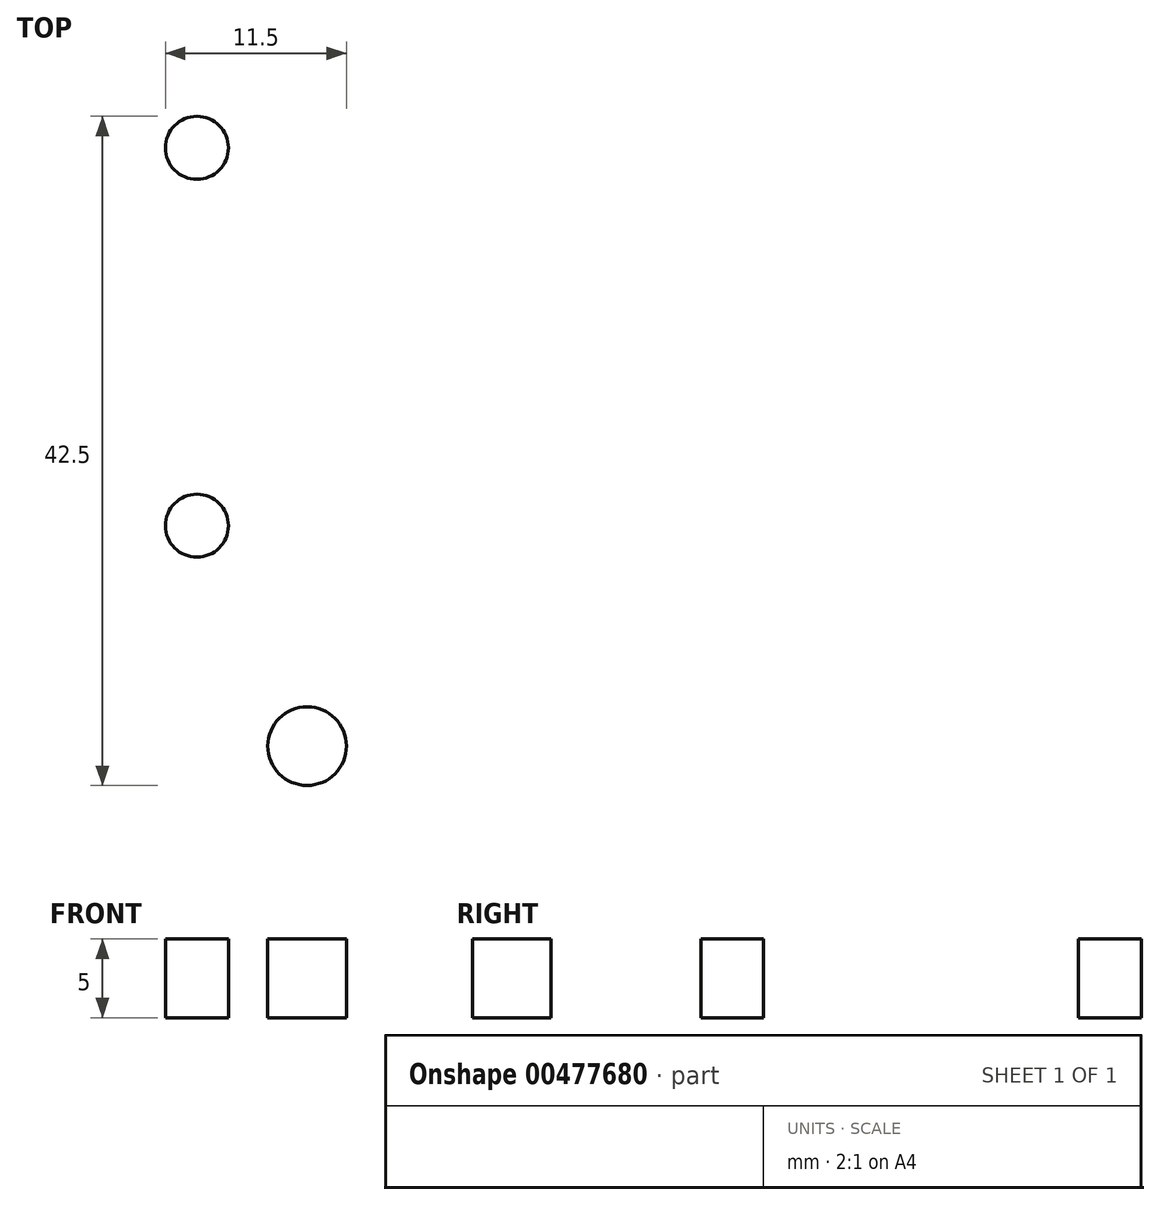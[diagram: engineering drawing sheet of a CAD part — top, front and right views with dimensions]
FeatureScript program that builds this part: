
annotation { "Feature Type Name" : "Feature", "Feature Type Description" : "" }
export const myFeature = defineFeature(function(context is Context, id is Id, definition is map)
    precondition{}
    {
        {
            var Q0;
            Q0=qCreatedBy(makeId("Top.planeOp"),FACE);
            var sketch = newSketch(context, id + "F0", { "sketchPlane" : qUnion([Q0])});
            skLineSegment(sketch, "E0.bottom", {"start": v(22.5, 27.5) * mm, "end": v(-22.5, 27.5) * mm});
            skLineSegment(sketch, "E0.top", {"start": v(22.5, -27.5) * mm, "end": v(-22.5, -27.5) * mm});
            skLineSegment(sketch, "E0.left", {"start": v(22.5, 27.5) * mm, "end": v(22.5, -27.5) * mm});
            skLineSegment(sketch, "E0.right", {"start": v(-22.5, 27.5) * mm, "end": v(-22.5, -27.5) * mm});
            skPoint(sketch, "E0.middle", {"position": v(0, 0) * mm});
            skSolve(sketch);
        }
        {
            var Q0;
            Q0=makeQuery(id+"F0.imprint","IMPRINT",FACE,{"disambiguationData":[TD([[makeQuery(id+"F0.imprint","IMPRINT",EDGE,{"derivedFrom":sQuery(id+"F0.wireOp",EDGE,"E0.bottom")}),1.0]])]});
            extrude(context, id + "F1", {"entities" : qUnion([Q0]), "depth" : 5 * mm});
        }
        {
            var Q0;
            Q0=makeQuery(id+"F1.opExtrude","CAP_FACE",FACE,{"disambiguationData":[OSD([sQuery(id+"F0.wireOp",EDGE,"E0.bottom"),sQuery(id+"F0.wireOp",EDGE,"E0.top"),sQuery(id+"F0.wireOp",EDGE,"E0.left"),sQuery(id+"F0.wireOp",EDGE,"E0.right")])],"isStart":false});
            var sketch = newSketch(context, id + "F2", { "sketchPlane" : qUnion([Q0])});
            skPoint(sketch, "E1.middle", {"position": v(0, 10.5) * mm});
            skCircle(sketch, "E2", {"center": v(-9, -3.5) * mm, "radius": 2 * mm});
            skCircle(sketch, "E3.MirrorC", {"center": v(9, 20.5) * mm, "radius": 2 * mm});
            skCircle(sketch, "E4.MirrorC", {"center": v(9, -3.5) * mm, "radius": 2 * mm});
            skCircle(sketch, "E5.MirrorC", {"center": v(-9, 20.5) * mm, "radius": 2 * mm});
            skCircle(sketch, "E6", {"center": v(-16, -17.5) * mm, "radius": 2.5 * mm});
            skCircle(sketch, "E7.MirrorC", {"center": v(16, -17.5) * mm, "radius": 2.5 * mm});
            skSolve(sketch);
        }
        {
            var Q0;
            Q0=makeQuery(id+"F2.imprint","IMPRINT",FACE,{"disambiguationData":[TD([[makeQuery(id+"F2.imprint","IMPRINT",EDGE,{"derivedFrom":sQuery(id+"F2.wireOp",EDGE,"E5.MirrorC")}),1.0]])]});
            var Q1;
            Q1=makeQuery(id+"F2.imprint","IMPRINT",FACE,{"disambiguationData":[TD([[makeQuery(id+"F2.imprint","IMPRINT",EDGE,{"derivedFrom":sQuery(id+"F2.wireOp",EDGE,"E3.MirrorC")}),-1.0]])]});
            var Q2;
            Q2=makeQuery(id+"F2.imprint","IMPRINT",FACE,{"disambiguationData":[TD([[makeQuery(id+"F2.imprint","IMPRINT",EDGE,{"derivedFrom":sQuery(id+"F2.wireOp",EDGE,"E2")}),1.0]])]});
            var Q3;
            Q3=makeQuery(id+"F2.imprint","IMPRINT",FACE,{"disambiguationData":[TD([[makeQuery(id+"F2.imprint","IMPRINT",EDGE,{"derivedFrom":sQuery(id+"F2.wireOp",EDGE,"E6")}),1.0]])]});
            var Q4;
            Q4=makeQuery(id+"F2.imprint","IMPRINT",FACE,{"disambiguationData":[TD([[makeQuery(id+"F2.imprint","IMPRINT",EDGE,{"derivedFrom":sQuery(id+"F2.wireOp",EDGE,"E4.MirrorC")}),-1.0]])]});
            var Q5;
            Q5=makeQuery(id+"F2.imprint","IMPRINT",FACE,{"disambiguationData":[TD([[makeQuery(id+"F2.imprint","IMPRINT",EDGE,{"derivedFrom":sQuery(id+"F2.wireOp",EDGE,"E7.MirrorC")}),-1.0]])]});
            extrude(context, id + "F3", {"entities" : qUnion([Q0, Q1, Q2, Q3, Q4, Q5]), "operationType" : NewBodyOperationType.REMOVE, "endBound" : BoundingType.THROUGH_ALL, "oppositeDirection" : true, "depth" : 25 * mm});
        }
    });
